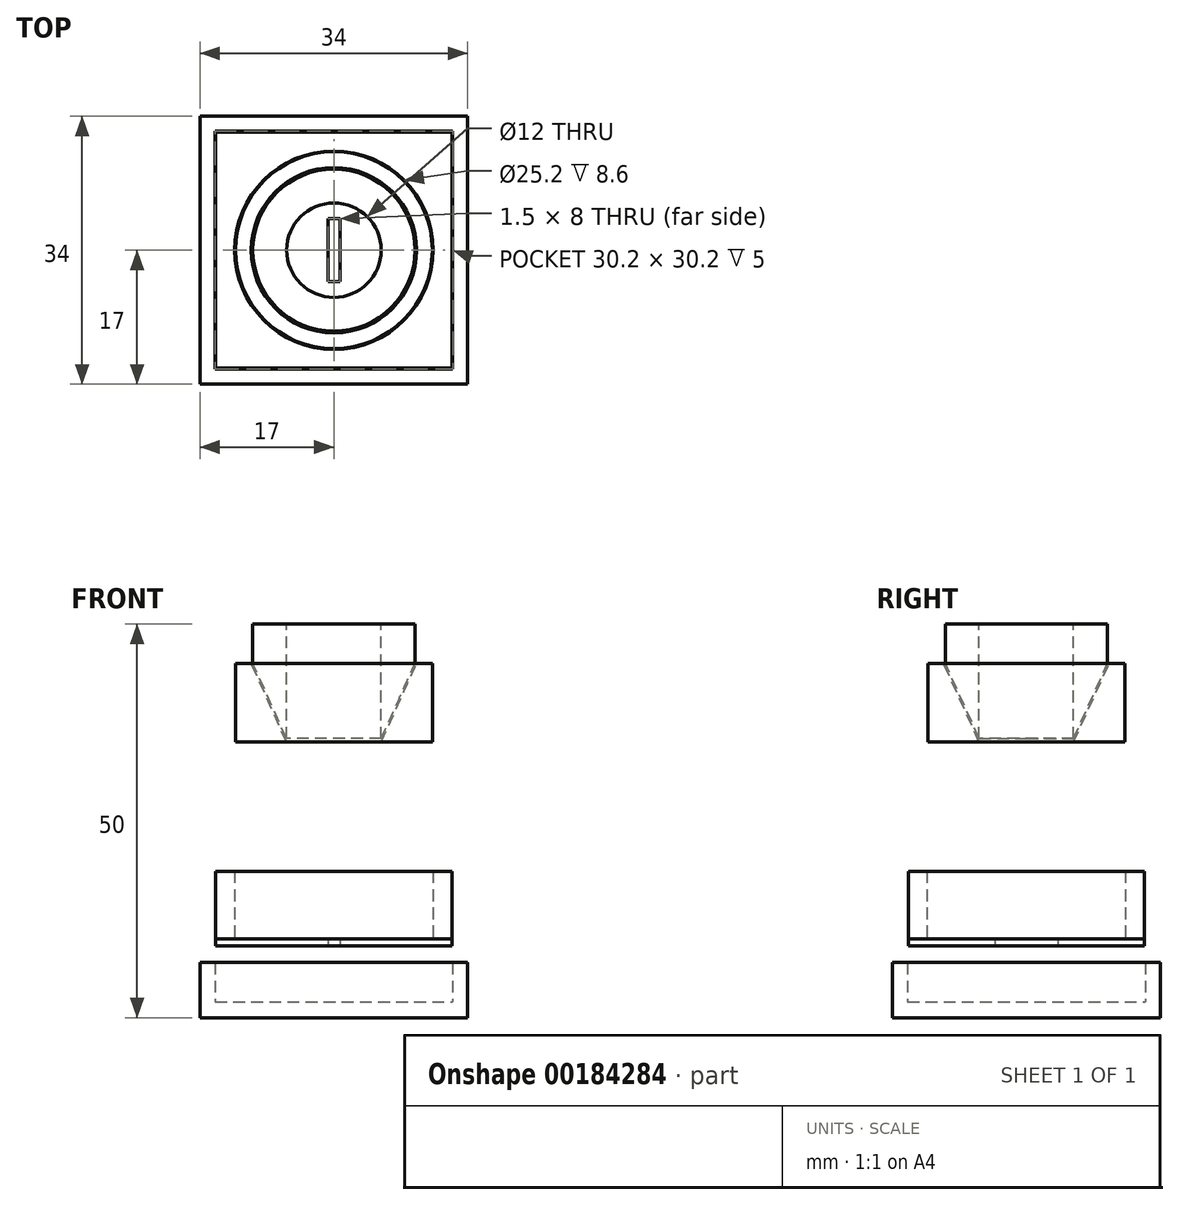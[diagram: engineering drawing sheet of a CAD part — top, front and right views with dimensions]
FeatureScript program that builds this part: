
annotation { "Feature Type Name" : "Feature", "Feature Type Description" : "" }
export const myFeature = defineFeature(function(context is Context, id is Id, definition is map)
    precondition{}
    {
        {
            assignVariable(context, id + "F0", {"name" : "dMaskThick", "anyValue" : .9});
        }
        {
            assignVariable(context, id + "F1", {"name" : "outerRingHeight", "anyValue" : 10});
        }
        {
            assignVariable(context, id + "F2", {"name" : "bottomLip", "anyValue" : .5});
        }
        {
            assignVariable(context, id + "F3", {"name" : "innerSquareHeight", "anyValue" : getVariable(context, 'outerRingHeight') - getVariable(context, 'dMaskThick') - getVariable(context, 'bottomLip')});
        }
        {
            var Q0;
            Q0=qCreatedBy(makeId("Right.planeOp"),FACE);
            var sketch = newSketch(context, id + "F4", { "sketchPlane" : qUnion([Q0])});
            skLineSegment(sketch, "E0.bottom", {"start": v(10.5, 10) * mm, "end": v(12.5, 10) * mm});
            skLineSegment(sketch, "E0.top", {"start": v(6, 0) * mm, "end": v(12.5, 0) * mm});
            skLineSegment(sketch, "E0.right", {"start": v(12.5, 10) * mm, "end": v(12.5, 0) * mm});
            skLineSegment(sketch, "E1", {"start": v(10.5, 10) * mm, "end": v(6, 0) * mm});
            skLineSegment(sketch, "E2", {"start": v(0, 0) * mm, "end": v(0, 15) * mm});
            skLineSegment(sketch, "E3", {"start": v(0, 15) * mm, "end": v(10.3, 15) * mm});
            skLineSegment(sketch, "E4", {"start": v(10.3, 15) * mm, "end": v(10.3, 10) * mm});
            skLineSegment(sketch, "E5", {"start": v(10.3, 10) * mm, "end": v(5.8, 0) * mm});
            skLineSegment(sketch, "E6", {"start": v(5.8, 0) * mm, "end": v(0, 0) * mm});
            skLineSegment(sketch, "E7", {"start": v(0, 23.44) * mm, "end": v(0, -7.5) * mm, "construction": true});
            skSolve(sketch);
        }
        {
            var Q0;
            Q0=qSketchRegion(id+"F4",true);
            var Q1;
            Q1=sQuery(id+"F4.wireOp",EDGE,"E7");
            revolve(context, id + "F5", {"entities" : qUnion([Q0]), "axis" : qUnion([Q1]), "revolveType" : RevolveType.FULL});
        }
        {
            var Q0;
            Q0=makeQuery(id+"F5.opRevolve","SWEPT_FACE",FACE,{"disambiguationData":[OSD([sQuery(id+"F4.wireOp",EDGE,"E3")])]});
            var sketch = newSketch(context, id + "F6", { "sketchPlane" : qUnion([Q0])});
            skCircle(sketch, "E8", {"center": v(0, 0) * mm, "radius": 6 * mm});
            skSolve(sketch);
        }
        {
            var Q0;
            Q0=makeQuery(id+"F6.imprint","IMPRINT",FACE,{"disambiguationData":[TD([[makeQuery(id+"F6.imprint","IMPRINT",EDGE,{"derivedFrom":sQuery(id+"F6.wireOp",EDGE,"E8")}),1.0]])]});
            var Q1;
            Q1=makeQuery(id+"F5.opRevolve","SWEPT_FACE",FACE,{"disambiguationData":[OSD([sQuery(id+"F4.wireOp",EDGE,"E0.top")])]});
            extrude(context, id + "F7", {"entities" : qUnion([Q0]), "operationType" : NewBodyOperationType.REMOVE, "endBound" : BoundingType.UP_TO_SURFACE, "oppositeDirection" : true, "endBoundEntityFace" : qUnion([Q1]), "depth" : 25 * mm});
        }
        {
            var Q0;
            Q0=qCreatedBy(makeId("Top.planeOp"),FACE);
            cPlane(context, id + "F8", {"entities" : qUnion([Q0]), "cplaneType" : CPlaneType.OFFSET, "offset" : 25 * mm, "oppositeDirection" : true, "width" : 150 * mm, "height" : 150 * mm});
        }
        {
            var Q0;
            Q0=qCreatedBy(id+"F8.planeOp",FACE);
            var sketch = newSketch(context, id + "F9", { "sketchPlane" : qUnion([Q0])});
            skCircle(sketch, "E9", {"center": v(0, 0) * mm, "radius": 12.6 * mm});
            skLineSegment(sketch, "E10.bottom", {"start": v(15, 15) * mm, "end": v(-15, 15) * mm});
            skLineSegment(sketch, "E10.top", {"start": v(15, -15) * mm, "end": v(-15, -15) * mm});
            skLineSegment(sketch, "E10.left", {"start": v(15, 15) * mm, "end": v(15, -15) * mm});
            skLineSegment(sketch, "E10.right", {"start": v(-15, 15) * mm, "end": v(-15, -15) * mm});
            skSolve(sketch);
        }
        {
            var Q0;
            Q0=makeQuery(id+"F9.imprint","IMPRINT",FACE,{"disambiguationData":[TD([[makeQuery(id+"F9.imprint","IMPRINT",EDGE,{"derivedFrom":sQuery(id+"F9.wireOp",EDGE,"E9")}),-1.0]])]});
            extrude(context, id + "F10", {"entities" : qUnion([Q0]), "depth" : (getVariable(context, 'innerSquareHeight')) * mm});
        }
        {
            var Q0;
            Q0=makeQuery(id+"F9.imprint","IMPRINT",FACE,{"disambiguationData":[TD([[makeQuery(id+"F9.imprint","IMPRINT",EDGE,{"derivedFrom":sQuery(id+"F9.wireOp",EDGE,"E9")}),1.0]])]});
            var Q1;
            Q1=makeQuery(id+"F9.imprint","IMPRINT",FACE,{"disambiguationData":[TD([[makeQuery(id+"F9.imprint","IMPRINT",EDGE,{"derivedFrom":sQuery(id+"F9.wireOp",EDGE,"E9")}),-1.0]])]});
            extrude(context, id + "F11", {"entities" : qUnion([Q0, Q1]), "oppositeDirection" : true, "depth" : (getVariable(context, 'dMaskThick')) * mm});
        }
        {
            var Q0;
            Q0=makeQuery(id+"F11.opExtrude","CAP_FACE",FACE,{"disambiguationData":[OSD([sQuery(id+"F9.wireOp",EDGE,"E10.bottom"),sQuery(id+"F9.wireOp",EDGE,"E10.top"),sQuery(id+"F9.wireOp",EDGE,"E10.left"),sQuery(id+"F9.wireOp",EDGE,"E10.right")])],"isStart":false});
            var sketch = newSketch(context, id + "F12", { "sketchPlane" : qUnion([Q0])});
            skLineSegment(sketch, "E11.bottom", {"start": v(0.75, 4) * mm, "end": v(-0.75, 4) * mm});
            skLineSegment(sketch, "E11.top", {"start": v(0.75, -4) * mm, "end": v(-0.75, -4) * mm});
            skLineSegment(sketch, "E11.left", {"start": v(0.75, 4) * mm, "end": v(0.75, -4) * mm});
            skLineSegment(sketch, "E11.right", {"start": v(-0.75, 4) * mm, "end": v(-0.75, -4) * mm});
            skPoint(sketch, "E11.middle", {"position": v(0, 0) * mm});
            skLineSegment(sketch, "E12", {"start": v(0, 4.63) * mm, "end": v(0, -4.8) * mm, "construction": true});
            skLineSegment(sketch, "E13", {"start": v(5.46, 0) * mm, "end": v(-5.8, 0) * mm, "construction": true});
            skSolve(sketch);
        }
        {
            var Q0;
            Q0=makeQuery(id+"F12.imprint","IMPRINT",FACE,{"disambiguationData":[TD([[makeQuery(id+"F12.imprint","IMPRINT",EDGE,{"derivedFrom":sQuery(id+"F12.wireOp",EDGE,"E11.bottom")}),1.0]])]});
            var Q1;
            Q1=makeQuery(id+"F11.opExtrude","CAP_FACE",FACE,{"disambiguationData":[OSD([sQuery(id+"F9.wireOp",EDGE,"E10.bottom"),sQuery(id+"F9.wireOp",EDGE,"E10.top"),sQuery(id+"F9.wireOp",EDGE,"E10.left"),sQuery(id+"F9.wireOp",EDGE,"E10.right")])],"isStart":true});
            extrude(context, id + "F13", {"entities" : qUnion([Q0]), "operationType" : NewBodyOperationType.REMOVE, "endBound" : BoundingType.UP_TO_SURFACE, "oppositeDirection" : true, "endBoundEntityFace" : qUnion([Q1]), "depth" : 25 * mm});
        }
        {
            var Q0;
            Q0=qCreatedBy(id+"F8.planeOp",FACE);
            cPlane(context, id + "F14", {"entities" : qUnion([Q0]), "cplaneType" : CPlaneType.OFFSET, "offset" : 10 * mm, "oppositeDirection" : true, "width" : 150 * mm, "height" : 150 * mm});
        }
        {
            var Q0;
            Q0=qCreatedBy(id+"F14.planeOp",FACE);
            var sketch = newSketch(context, id + "F15", { "sketchPlane" : qUnion([Q0])});
            skLineSegment(sketch, "E14.bottom", {"start": v(15.1, 15.1) * mm, "end": v(-15.1, 15.1) * mm});
            skLineSegment(sketch, "E14.top", {"start": v(15.1, -15.1) * mm, "end": v(-15.1, -15.1) * mm});
            skLineSegment(sketch, "E14.left", {"start": v(15.1, 15.1) * mm, "end": v(15.1, -15.1) * mm});
            skLineSegment(sketch, "E14.right", {"start": v(-15.1, 15.1) * mm, "end": v(-15.1, -15.1) * mm});
            skPoint(sketch, "E14.middle", {"position": v(0, 0) * mm});
            skLineSegment(sketch, "E15.bottom", {"start": v(17, 17) * mm, "end": v(-17, 17) * mm});
            skLineSegment(sketch, "E15.top", {"start": v(17, -17) * mm, "end": v(-17, -17) * mm});
            skLineSegment(sketch, "E15.left", {"start": v(17, 17) * mm, "end": v(17, -17) * mm});
            skLineSegment(sketch, "E15.right", {"start": v(-17, 17) * mm, "end": v(-17, -17) * mm});
            skSolve(sketch);
        }
        {
            var Q0;
            Q0=qSketchRegion(id+"F15",true);
            var Q1;
            Q1=makeQuery(id+"F15.imprint","IMPRINT",FACE,{"disambiguationData":[TD([[makeQuery(id+"F15.imprint","IMPRINT",EDGE,{"derivedFrom":sQuery(id+"F15.wireOp",EDGE,"E14.bottom")}),1.0]])]});
            extrude(context, id + "F16", {"entities" : qUnion([Q0, Q1]), "depth" : 2 * mm});
        }
        {
            var Q0;
            Q0=makeQuery(id+"F15.imprint","IMPRINT",FACE,{"disambiguationData":[TD([[makeQuery(id+"F15.imprint","IMPRINT",EDGE,{"derivedFrom":sQuery(id+"F15.wireOp",EDGE,"E14.bottom")}),-1.0]])]});
            extrude(context, id + "F17", {"entities" : qUnion([Q0]), "operationType" : NewBodyOperationType.ADD, "depth" : 7 * mm});
        }
    });
